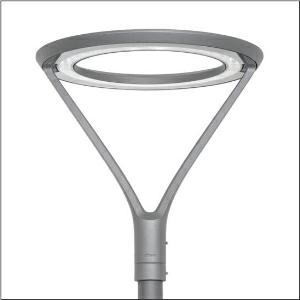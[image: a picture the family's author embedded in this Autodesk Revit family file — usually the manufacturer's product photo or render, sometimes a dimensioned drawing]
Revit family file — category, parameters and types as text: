
# Revit family: dl_r__20___p1_0a_5xa512832r008_6e66
name_source: partatom
category: Lighting Fixtures
units: mm (PartAtom-declared; Revit-internal decimal feet)

## family parameters
Cut with Voids When Loaded = No
Host = Face
Light Source = No
Part Type = Normal
Room Calculation Point = No
Round Connector Dimension = Use Diameter
Shared = No

## types (1)
- --- (1 x LED, 3030 lm, 30.4 W, 2200K)
    Apparent Load = 30 VA
    CIE Flux Codes = 31 71 96 100 100
    Color Rendering = 70
    Color Temperature = 2200K
    Default Elevation = 1800 mm
    Description = DL® 20, mast luminaire, primary light control with cycle path optic, highly specular, primary optical cover: cover, of toughened safety glass of clear glass with excellent transmission level, light distribution: P1.0a, light emission: direct distribution, primary light characteristic: asymmetric, installation type: post-top, LED, High Power LED, rated luminous flux: 3.060lm, luminous efficacy: 86lm/W, light colour: 722, colour temperature: 2200K, control gear: ECG Plus, control: flexible luminous flux parameterisation, time-dependent luminous flux control, constant luminous flux control, digital communication interface, power reduction, overheat protection, electronic power reduction, mains connection: 230..240V, 50/60Hz, connection cable pre-assembled, cable length: 5m, start of lifetime: 36W, end of service life: 36W, reduction: 17W, luminaire housing, upper part, of cast aluminium, powder-coated, Siteco® metallic grey (DB 702S), diameter: 690mm, height: 690mm, spigot size: 76mm (post-top), luminaire housing, of cast aluminium, powder-coated, Siteco® metallic grey (DB 702S), equipment: standard, protection rating (complete): IP66, insulation class (complete): insulation class II (safety insulation), certification: CE, ENEC, VDE, impact resistance: IK08, permissible operating ambient temperature: -25..+35°C, standard-compliant lighting for roads and squares, packaging unit: 1 piece

Light Distribution: P1.0a
    Height = 690 mm
    Lamp = 1 x LED
    Lamp Light Flux = 3030 lm
    Lamp Power = 30.4 W
    Lamp count = 1
    Length = 690 mm
    Luminous efficacy = 100 lm/W
    Manufacturer = Siteco
    ModVariant = No
    Model = 5XA512832R008
    Number of Poles = 1
    OnlyDefault = Yes
    Power Factor = 1
    Product Name = DL® 20 | P1.0a
    Product group = mast luminaire | pylon top
    ProductGroupID = 6100
    Protection Class = Protection class II
    Protection Degree = IP 66
    RLX_Detail_Level = 1
    RLX_Emergency_Light_Flux = 0 lm
    RLX_Emergency_Type = 0
    RLX_Emergency_Type_DB = No
    RlxData = <blob elided: 206493 chars, md5=b6002ff4>
    Socket = socket
    Standby Power = 0 W
    System Light Flux = 3030 lm
    System Power = 30 W
    Type Comments = factory setting: luminous flux: 100 % | dim-lin: 254 | 412 mA
    Type Image = l_1006001.jpg
    URL = http://relux.com
    VarID = @adj_009449
    Voltage = 0 V
    Weight = 0.00 kg
    Width = 0 mm  [stored 0 ft]

note: [stored X ft] marks values corroborated as IEEE doubles in the binary element streams (Revit-internal decimal feet)

## geometry (parser evidence)
native form markers: Blend x4, Sweep x10
no freeform markers — native parametric forms only
